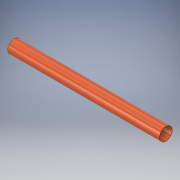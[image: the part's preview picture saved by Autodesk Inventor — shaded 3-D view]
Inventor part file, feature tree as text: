
AUTODESK INVENTOR PART (.ipt)
format: ipt  version: 2017 SP1 (Build 210196100, 196)  size: 99,840 bytes
history: native  units: in
note: dims shown in document units (in); Inventor stores cm internally (conversion verified against a paired STEP export)
features: extrude x1, sketch x1
ambient origin geometry x8: Origin, YZ Plane, XZ Plane, XY Plane, X Axis, Y Axis, Z Axis, Center Point
bodies: Solid1 (feature_tree)
feature tree (2):
  extrude  "Extrusion1"  Depth=86.7in
  sketch  "Sketch1"  dims[d0=7.4in d1=7.15in d2=86.7in d3=0.0in]
